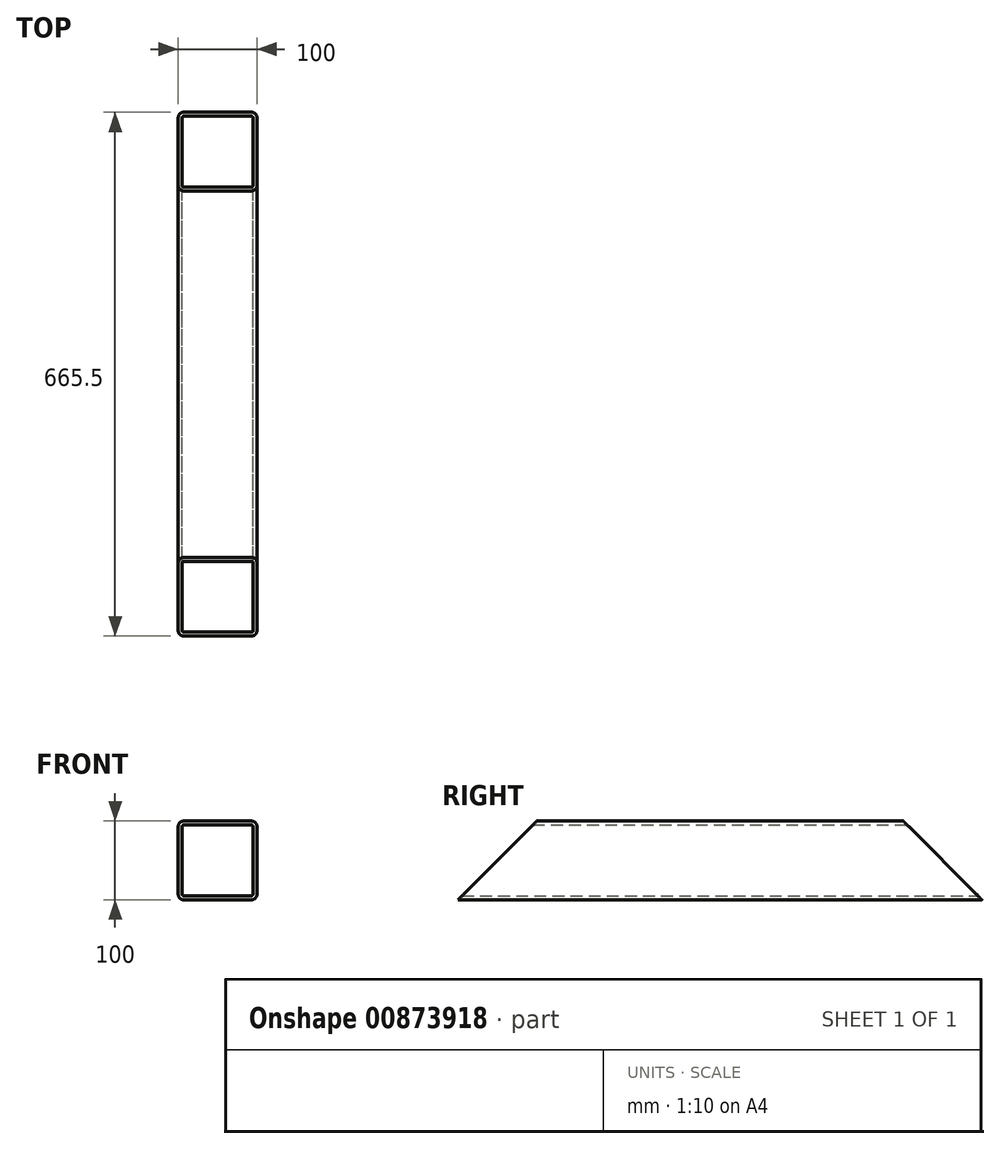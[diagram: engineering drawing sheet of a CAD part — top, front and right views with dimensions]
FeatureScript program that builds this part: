
annotation { "Feature Type Name" : "Feature", "Feature Type Description" : "" }
export const myFeature = defineFeature(function(context is Context, id is Id, definition is map)
    precondition{}
    {
        {
            var Q0;
            Q0=qCreatedBy(makeId("Front.planeOp"),FACE);
            var sketch = newSketch(context, id + "F0", { "sketchPlane" : qUnion([Q0])});
            skLineSegment(sketch, "E0.bottom", {"start": v(43, 50) * mm, "end": v(-43, 50) * mm});
            skLineSegment(sketch, "E0.top", {"start": v(43, -50) * mm, "end": v(-43, -50) * mm});
            skLineSegment(sketch, "E0.left", {"start": v(50, 43) * mm, "end": v(50, -43) * mm});
            skLineSegment(sketch, "E0.right", {"start": v(-50, 43) * mm, "end": v(-50, -43) * mm});
            skPoint(sketch, "E0.middle", {"position": v(0, 0) * mm});
            skPoint(sketch, "E1.visualSharp", {"position": v(-50, 50) * mm});
            skArc(sketch, "E1.filletArc", {"start": v(-43, 50) * mm, "mid": v(-47.95, 47.95) * mm, "end": v(-50, 43) * mm});
            skPoint(sketch, "E2.visualSharp", {"position": v(50, 50) * mm});
            skArc(sketch, "E2.filletArc", {"start": v(50, 43) * mm, "mid": v(47.95, 47.95) * mm, "end": v(43, 50) * mm});
            skPoint(sketch, "E3.visualSharp", {"position": v(-50, -50) * mm});
            skArc(sketch, "E3.filletArc", {"start": v(-50, -43) * mm, "mid": v(-47.95, -47.95) * mm, "end": v(-43, -50) * mm});
            skPoint(sketch, "E4.visualSharp", {"position": v(50, -50) * mm});
            skArc(sketch, "E4.filletArc", {"start": v(43, -50) * mm, "mid": v(47.95, -47.95) * mm, "end": v(50, -43) * mm});
            skLineSegment(sketch, "E5.0", {"start": v(43, -45) * mm, "end": v(-43, -45) * mm});
            skArc(sketch, "E5.1", {"start": v(-45, -43) * mm, "mid": v(-44.41, -44.41) * mm, "end": v(-43, -45) * mm});
            skArc(sketch, "E5.2", {"start": v(43, -45) * mm, "mid": v(44.41, -44.41) * mm, "end": v(45, -43) * mm});
            skLineSegment(sketch, "E5.3", {"start": v(-45, 43) * mm, "end": v(-45, -43) * mm});
            skLineSegment(sketch, "E5.4", {"start": v(45, 43) * mm, "end": v(45, -43) * mm});
            skArc(sketch, "E5.5", {"start": v(45, 43) * mm, "mid": v(44.41, 44.41) * mm, "end": v(43, 45) * mm});
            skLineSegment(sketch, "E5.6", {"start": v(43, 45) * mm, "end": v(-43, 45) * mm});
            skArc(sketch, "E5.7", {"start": v(-43, 45) * mm, "mid": v(-44.41, 44.41) * mm, "end": v(-45, 43) * mm});
            skSolve(sketch);
        }
        {
            var Q0;
            Q0=makeQuery(id+"F0.imprint","IMPRINT",FACE,{"disambiguationData":[TD([[makeQuery(id+"F0.imprint","IMPRINT",EDGE,{"derivedFrom":sQuery(id+"F0.wireOp",EDGE,"E0.bottom")}),1.0]])]});
            extrude(context, id + "F1", {"entities" : qUnion([Q0]), "depth" : 665.5 * mm, "offsetDistance" : 25 * mm, "symmetric" : true});
        }
        {
            var Q0;
            Q0=makeQuery(id+"F1.opExtrude","SWEPT_FACE",FACE,{"disambiguationData":[OSD([sQuery(id+"F0.wireOp",EDGE,"E0.left")])]});
            var sketch = newSketch(context, id + "F2", { "sketchPlane" : qUnion([Q0])});
            skLineSegment(sketch, "E6.top", {"start": v(232.75, 50) * mm, "end": v(332.75, 50) * mm});
            skPoint(sketch, "E6.middle", {"position": v(332.75, 0) * mm});
            skLineSegment(sketch, "E7", {"start": v(332.75, -50) * mm, "end": v(232.75, 50) * mm});
            skLineSegment(sketch, "E8", {"start": v(332.75, -50) * mm, "end": v(332.75, 50) * mm});
            skLineSegment(sketch, "E9.MirrorCS", {"start": v(-232.75, 50) * mm, "end": v(-332.75, 50) * mm});
            skLineSegment(sketch, "E10.MirrorCS", {"start": v(-332.75, -50) * mm, "end": v(-332.75, 50) * mm});
            skPoint(sketch, "E11.MirrorP", {"position": v(-332.75, 0) * mm});
            skLineSegment(sketch, "E12.MirrorCS", {"start": v(-332.75, -50) * mm, "end": v(-232.75, 50) * mm});
            skSolve(sketch);
        }
        {
            var Q0;
            Q0=qSketchRegion(id+"F2",true);
            extrude(context, id + "F3", {"entities" : qUnion([Q0]), "operationType" : NewBodyOperationType.REMOVE, "endBound" : BoundingType.THROUGH_ALL, "oppositeDirection" : true, "depth" : 25 * mm, "offsetDistance" : 25 * mm});
        }
    });
